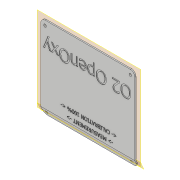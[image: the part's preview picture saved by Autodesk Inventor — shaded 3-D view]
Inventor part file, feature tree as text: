
AUTODESK INVENTOR PART (.ipt)
format: ipt  version: 2019.4 (Build 234330000, 330)  size: 836,608 bytes
history: native  units: mm
features: extrude x3, sketch x3, plane x2, reference x2, other x2, projected_geometry x1
ambient origin geometry x8: Origin, YZ Plane, XZ Plane, XY Plane, X Axis, Y Axis, Z Axis, Center Point
bodies: Solid1 (feature_tree)
feature tree (13):
  plane  "Work Plane1"
  extrude  "Extrusion1"  Depth=1.5mm TaperAngle=0.0deg
  plane  "Work Plane2"
  extrude  "Extrusion2"  [1 undecoded]
  extrude  "Extrusion3"  [1 undecoded]
  sketch  "Sketch1"  dims[d0=1.5mm d1=0.0mm d2=1.5mm d3=0.0mm]
  reference  "Reference1"
  sketch  "Sketch2"  dims[d4=0.5mm d5=0.0mm]
  reference  "Reference2"
  sketch  "Sketch3"
  projected_geometry  "Projected Loop1"
  other  "Assemlby_OpenOxygen.iam"
  other  "03_OpenOxygen_Box:1"
note: 2 required parameter values undecoded (feature->parameter linkage not recoverable at this tier; creation-order binding heuristic only, values carry confidence <= 0.55)
